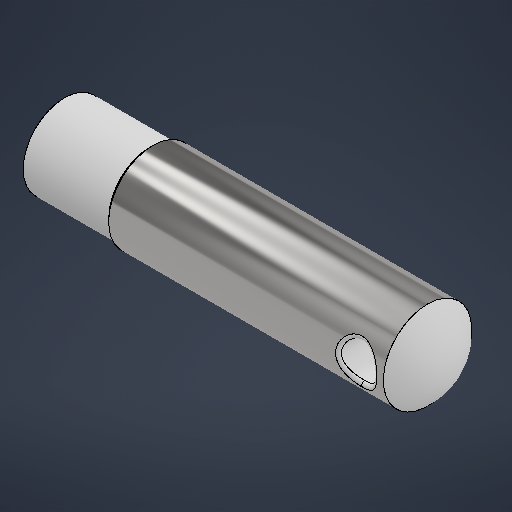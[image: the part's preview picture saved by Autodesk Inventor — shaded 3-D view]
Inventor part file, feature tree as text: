
AUTODESK INVENTOR PART (.ipt)
format: ipt  version: 2025.3 (Build 293356000, 356)  size: 289,792 bytes
history: native  units: mm
features: sketch x1, revolve x1, extrude x1, fillet x1, other x1
ambient origin geometry x8: Origin, YZ Plane, XZ Plane, XY Plane, X Axis, Y Axis, Z Axis, Center Point
bodies: Solid1 (feature_tree)
feature tree (5):
  sketch  "Sketch1"  dims[d0=10.2mm d3=15.0mm d5=60.0deg d6=50.0mm d8=15.0mm d9=10.0mm d10=6.0mm d11=360.0deg d12=65.0mm d13=0.5mm d14=0.5mm d15=57.0mm d16=0.0mm d17=0.0mm d18=0.5mm d19=14.0mm]
  revolve  "Revolution1"  [1 undecoded]
  extrude  "Extrusion1"  TaperAngle=60.0deg  [1 undecoded]
  fillet  "Fillet1"  Radius=50.0mm
  other  "Finish1"
note: 2 required parameter values undecoded (feature->parameter linkage not recoverable at this tier; creation-order binding heuristic only, values carry confidence <= 0.55)